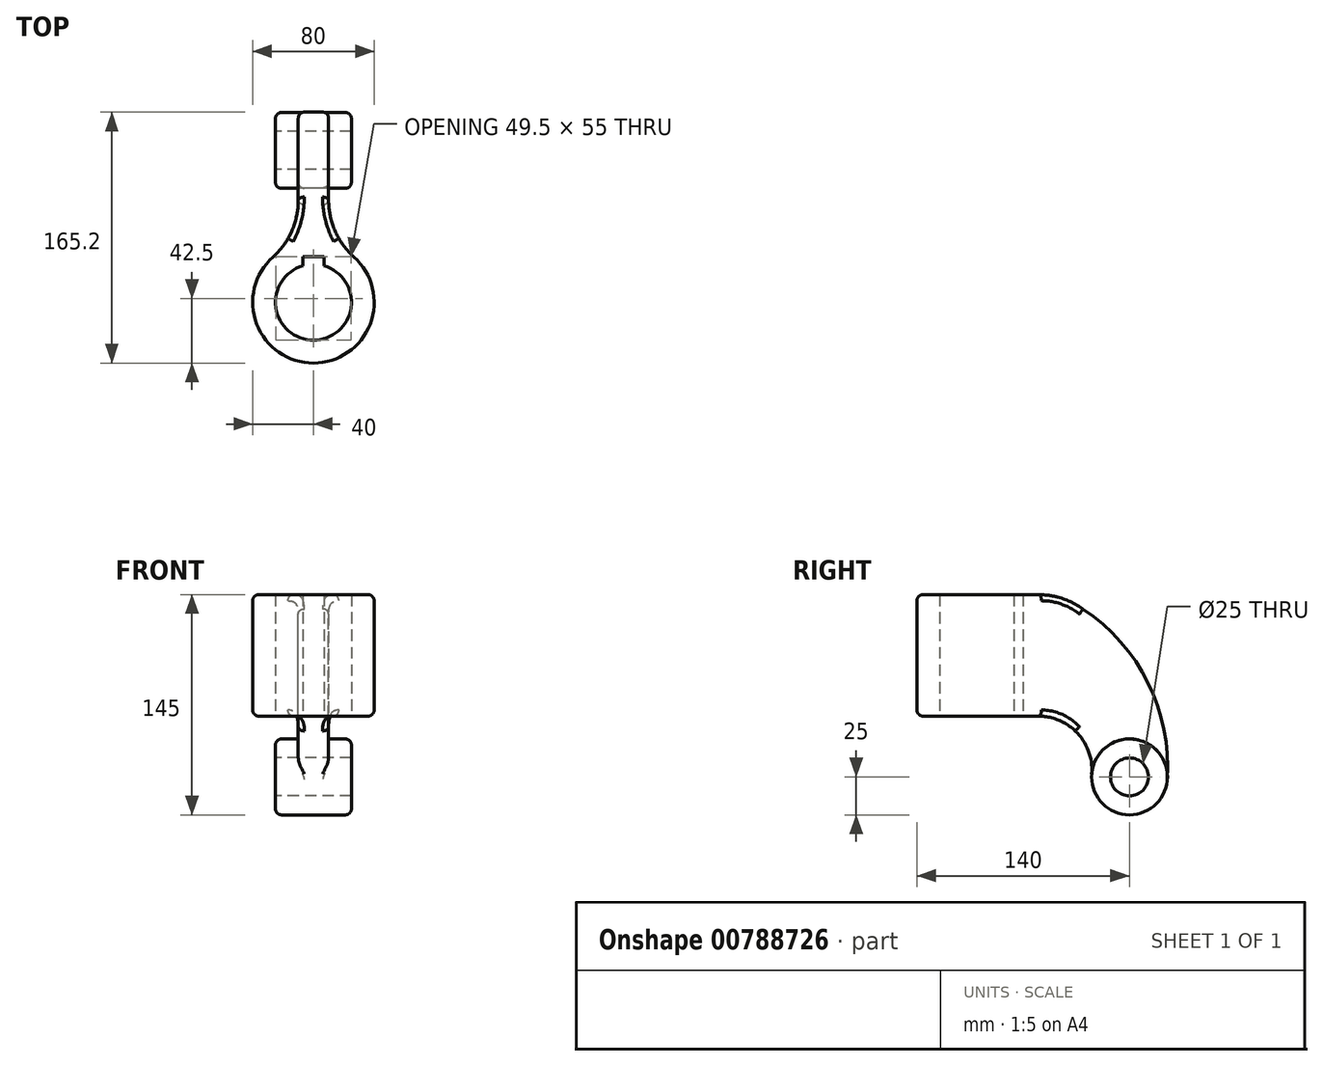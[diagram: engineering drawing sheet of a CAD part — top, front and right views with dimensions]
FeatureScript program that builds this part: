
annotation { "Feature Type Name" : "Feature", "Feature Type Description" : "" }
export const myFeature = defineFeature(function(context is Context, id is Id, definition is map)
    precondition{}
    {
        {
            var Q0;
            Q0=qCreatedBy(makeId("Top.planeOp"),FACE);
            var sketch = newSketch(context, id + "F0", { "sketchPlane" : qUnion([Q0])});
            skArc(sketch, "E0", {"start": v(-7, 24) * mm, "mid": v(0, -25) * mm, "end": v(7, 24) * mm});
            skCircle(sketch, "E1", {"center": v(0, 0) * mm, "radius": 40 * mm});
            skLineSegment(sketch, "E2.top", {"start": v(-7, 30) * mm, "end": v(7, 30) * mm});
            skLineSegment(sketch, "E2.left", {"start": v(-7, 24) * mm, "end": v(-7, 30) * mm});
            skLineSegment(sketch, "E2.right", {"start": v(7, 24) * mm, "end": v(7, 30) * mm});
            skPoint(sketch, "E3", {"position": v(0, 30) * mm});
            skSolve(sketch);
        }
        {
            var Q0;
            Q0=makeQuery(id+"F0.imprint","IMPRINT",FACE,{"disambiguationData":[TD([[makeQuery(id+"F0.imprint","IMPRINT",EDGE,{"derivedFrom":sQuery(id+"F0.wireOp",EDGE,"E1")}),1.0]])]});
            extrude(context, id + "F1", {"entities" : qUnion([Q0]), "depth" : 80 * mm, "offsetDistance" : 25 * mm});
        }
        {
            var Q0;
            Q0=qCreatedBy(makeId("Right.planeOp"),FACE);
            var sketch = newSketch(context, id + "F2", { "sketchPlane" : qUnion([Q0])});
            skLineSegment(sketch, "E4.0", {"start": v(-40, 80) * mm, "end": v(40, 80) * mm, "construction": true});
            skLineSegment(sketch, "E5.0", {"start": v(-40, 0) * mm, "end": v(40, 0) * mm, "construction": true});
            skArc(sketch, "E6", {"start": v(66.6, 72.34) * mm, "mid": v(53.84, 78.05) * mm, "end": v(40, 80) * mm});
            skCircle(sketch, "E7", {"center": v(100, -40) * mm, "radius": 12.5 * mm});
            skCircle(sketch, "E8", {"center": v(100, -40) * mm, "radius": 25 * mm});
            skArc(sketch, "E9", {"start": v(66.6, 72.34) * mm, "mid": v(111.43, 23.4) * mm, "end": v(124.95, -41.58) * mm});
            skArc(sketch, "E10", {"start": v(40, 0) * mm, "mid": v(65.86, -11.32) * mm, "end": v(75.08, -38) * mm});
            skLineSegment(sketch, "E11", {"start": v(40, 80) * mm, "end": v(40, 0) * mm});
            skSolve(sketch);
        }
        {
            var Q0;
            Q0=makeQuery(id+"F2.imprint","IMPRINT",FACE,{"disambiguationData":[TD([[makeQuery(id+"F2.imprint","IMPRINT",EDGE,{"derivedFrom":sQuery(id+"F2.wireOp",EDGE,"E6")}),1.0]])]});
            extrude(context, id + "F3", {"entities" : qUnion([Q0]), "endBound" : BoundingType.SYMMETRIC, "depth" : 20 * mm, "offsetDistance" : 25 * mm});
        }
        {
            var Q0;
            Q0=makeQuery(id+"F3.opExtrude","SWEPT_FACE",FACE,{"disambiguationData":[OSD([sQuery(id+"F2.wireOp",EDGE,"E11")])]});
            var Q1;
            Q1=makeQuery(id+"F1.opExtrude","SWEPT_FACE",FACE,{"disambiguationData":[OSD([sQuery(id+"F0.wireOp",EDGE,"E2.top")])]});
            extrude(context, id + "F4", {"entities" : qUnion([Q0]), "operationType" : NewBodyOperationType.ADD, "endBound" : BoundingType.UP_TO_SURFACE, "depth" : 25 * mm, "endBoundEntityFace" : qUnion([Q1]), "offsetDistance" : 25 * mm});
        }
        {
            var Q0;
            Q0=makeQuery(id+"F2.imprint","IMPRINT",FACE,{"disambiguationData":[TD([[makeQuery(id+"F2.imprint","IMPRINT",EDGE,{"derivedFrom":sQuery(id+"F2.wireOp",EDGE,"E7")}),-1.0]])]});
            extrude(context, id + "F5", {"entities" : qUnion([Q0]), "operationType" : NewBodyOperationType.ADD, "endBound" : BoundingType.SYMMETRIC, "depth" : 50 * mm, "offsetDistance" : 25 * mm});
        }
        {
            var Q0;
            {var subQ0=sQuery(id+"F2.wireOp",EDGE,"E11");Q0=makeQuery(id+"F4.boolean.opBoolean","INTERSECT",EDGE,{"derivedFrom":[makeQuery(id+"F1.opExtrude","SWEPT_FACE",FACE,{"disambiguationData":[OSD([sQuery(id+"F0.wireOp",EDGE,"E1")])]}),makeQuery(id+"F4.opExtrude","SWEPT_FACE",FACE,{"disambiguationData":[OSD([subQ0]),TDD([makeQuery(id+"F3.opExtrude","CAP_EDGE",EDGE,{"disambiguationData":[OSD([subQ0])],"isStart":false})])]})]});}
            var Q1;
            {var subQ0=sQuery(id+"F2.wireOp",EDGE,"E11");Q1=makeQuery(id+"F4.boolean.opBoolean","INTERSECT",EDGE,{"derivedFrom":[makeQuery(id+"F1.opExtrude","SWEPT_FACE",FACE,{"disambiguationData":[OSD([sQuery(id+"F0.wireOp",EDGE,"E1")])]}),makeQuery(id+"F4.opExtrude","SWEPT_FACE",FACE,{"disambiguationData":[OSD([subQ0]),TDD([makeQuery(id+"F3.opExtrude","CAP_EDGE",EDGE,{"disambiguationData":[OSD([subQ0])],"isStart":true})])]})]});}
            fillet(context, id + "F6", {"entities" : qUnion([Q0, Q1]), "radius" : 50 * mm, "tangentPropagation" : true, "allowEdgeOverflow" : false});
        }
        {
            var Q0;
            Q0=makeQuery(id+"F5.opExtrude","CAP_EDGE",EDGE,{"disambiguationData":[OSD([sQuery(id+"F2.wireOp",EDGE,"E8")])],"isStart":false});
            var Q1;
            Q1=makeQuery(id+"F5.opExtrude","CAP_EDGE",EDGE,{"disambiguationData":[OSD([sQuery(id+"F2.wireOp",EDGE,"E8")])],"isStart":true});
            var Q2;
            {var subQ0=sQuery(id+"F2.wireOp",EDGE,"E11");var subQ1=sQuery(id+"F0.wireOp",EDGE,"E1");Q2=makeQuery(id+"F6.opFillet","BLEND_EDGE",EDGE,{"blendedFrom":[makeQuery(id+"F4.boolean.opBoolean","INTERSECT",EDGE,{"derivedFrom":[makeQuery(id+"F1.opExtrude","SWEPT_FACE",FACE,{"disambiguationData":[OSD([subQ1])]}),makeQuery(id+"F4.opExtrude","SWEPT_FACE",FACE,{"disambiguationData":[OSD([subQ0]),TDD([makeQuery(id+"F3.opExtrude","CAP_EDGE",EDGE,{"disambiguationData":[OSD([subQ0])],"isStart":true})])]})]}),makeQuery(id+"F4.boolean.opBoolean","MERGE",FACE,{"derivedFrom":[makeQuery(id+"F1.opExtrude","CAP_FACE",FACE,{"disambiguationData":[OSD([sQuery(id+"F0.wireOp",EDGE,"E0"),subQ1,sQuery(id+"F0.wireOp",EDGE,"E2.top"),sQuery(id+"F0.wireOp",EDGE,"E2.left"),sQuery(id+"F0.wireOp",EDGE,"E2.right")])],"isStart":false}),makeQuery(id+"F4.opExtrude","SWEPT_FACE",FACE,{"disambiguationData":[OSD([sQuery(id+"F2.wireOp",EDGE,"E6"),subQ0])]})]})],"blendedInto":[makeQuery(id+"F4.boolean.opBoolean","MERGE",FACE,{"derivedFrom":[makeQuery(id+"F1.opExtrude","CAP_FACE",FACE,{"disambiguationData":[OSD([sQuery(id+"F0.wireOp",EDGE,"E0"),subQ1,sQuery(id+"F0.wireOp",EDGE,"E2.top"),sQuery(id+"F0.wireOp",EDGE,"E2.left"),sQuery(id+"F0.wireOp",EDGE,"E2.right")])],"isStart":false}),makeQuery(id+"F4.opExtrude","SWEPT_FACE",FACE,{"disambiguationData":[OSD([sQuery(id+"F2.wireOp",EDGE,"E6"),subQ0])]})]})]});}
            var Q3;
            Q3=makeQuery(id+"F3.opExtrude","CAP_EDGE",EDGE,{"disambiguationData":[OSD([sQuery(id+"F2.wireOp",EDGE,"E8")])],"isStart":false});
            var Q4;
            Q4=makeQuery(id+"F3.opExtrude","CAP_EDGE",EDGE,{"disambiguationData":[OSD([sQuery(id+"F2.wireOp",EDGE,"E8")])],"isStart":true});
            var Q5;
            Q5=makeQuery(id+"F1.opExtrude","CAP_EDGE",EDGE,{"disambiguationData":[OSD([sQuery(id+"F0.wireOp",EDGE,"E1")])],"isStart":true});
            fillet(context, id + "F7", {"entities" : qUnion([Q0, Q1, Q2, Q3, Q4, Q5]), "radius" : 4 * mm, "tangentPropagation" : true, "allowEdgeOverflow" : false});
        }
    });
